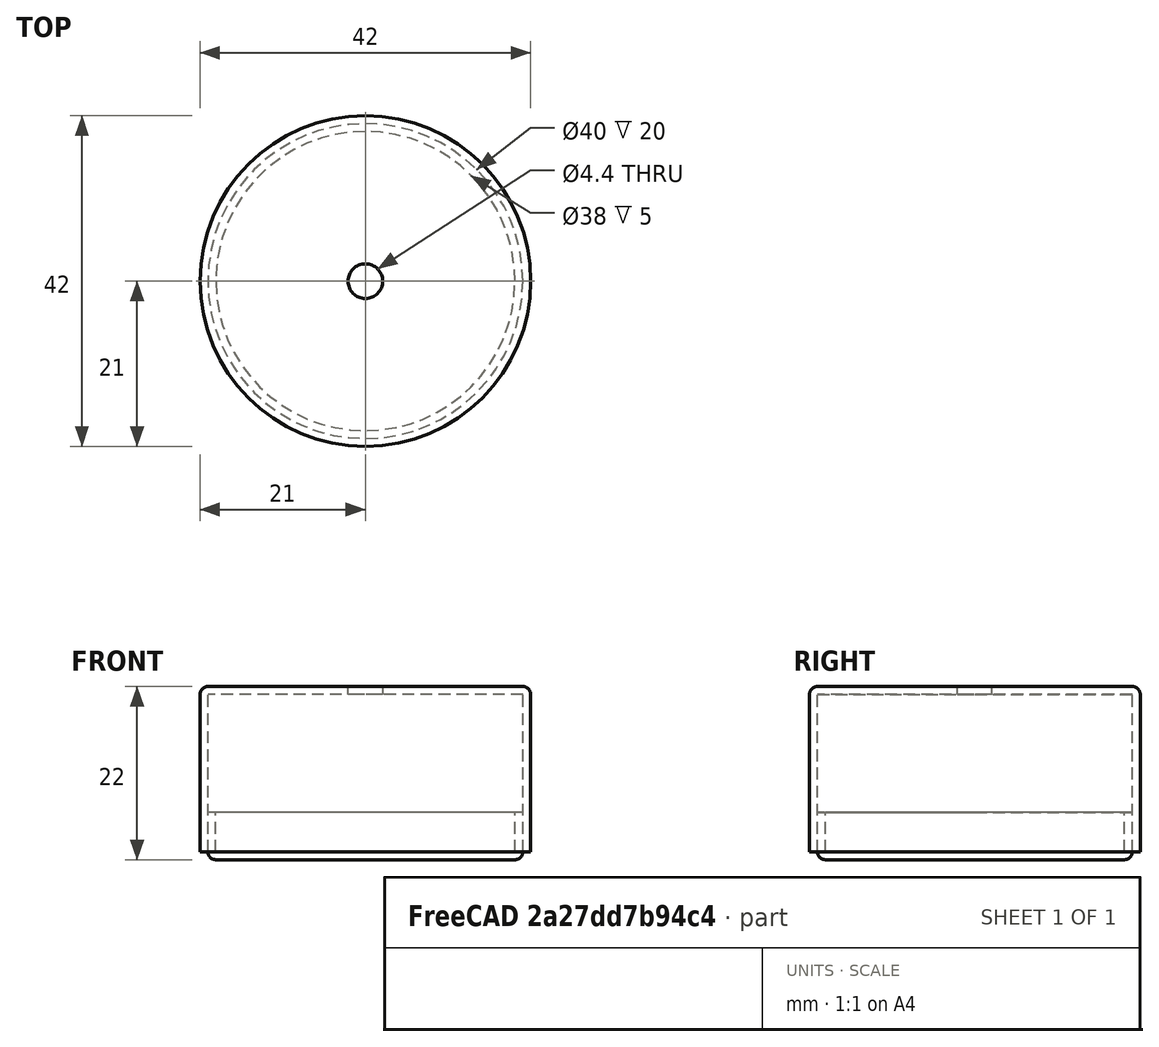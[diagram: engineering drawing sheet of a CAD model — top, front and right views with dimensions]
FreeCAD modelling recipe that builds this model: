
FCSTD DOCUMENT  (FreeCAD 0.19R)
Label: led_kerzenlicht
License: All rights reserved
LicenseURL: http://en.wikipedia.org/wiki/All_rights_reserved
objects: PartDesign::AdditiveCylinder×2, PartDesign::Thickness×2, PartDesign::Body×2, Sketcher::SketchObject×1, PartDesign::Pocket×1
note: 13 computed .brp shape members not serialized (recipe doc carries the construction recipe); baked Part::Feature solids carry a one-line shape summary decoded from their .brp

FEATURE [PartDesign::AdditiveCylinder] Cylinder
  Angle = 360
  AttacherType = Attacher::AttachEngine3D
  Height = 20
  Radius = 20
  Refine = true
FEATURE [PartDesign::Thickness] Thickness
  Base = -> Cylinder [Face3]
  BaseFeature = -> Cylinder
  Intersection = false
  Join = 0
  Mode = 0
  Refine = true
  SupportTransform = false
  Value = 1
FEATURE [Sketcher::SketchObject] Sketch
  FullyConstrained = true
  MapMode = 5
  Placement = pos=(0,0,21) rot=(0,0,1;0rad)
  Support = -> [Thickness]
  sketch-geometry (1):
    g0: Circle CenterX=0 CenterY=0 CenterZ=0 NormalX=0 NormalY=0 NormalZ=1 AngleXU=0 Radius=2.2
  constraints (2):
    c: Radius(g0) = 2.2
    c: Coincident(g0,g-1)
FEATURE [PartDesign::Pocket] Pocket
  BaseFeature = -> Thickness
  Length = 5
  Length2 = 100
  Profile = -> Sketch
  Refine = true
  Type = 1
FEATURE [PartDesign::Body] Body
  Group = -> [Cylinder,Thickness,Sketch,Pocket]
  Origin = -> Origin
  Tip = -> Pocket
FEATURE [PartDesign::AdditiveCylinder] Cylinder001
  Angle = 360
  AttacherType = Attacher::AttachEngine3D
  Height = 5
  Radius = 19
  Refine = true
FEATURE [PartDesign::Thickness] Thickness001
  Base = -> Cylinder001 [Face2]
  BaseFeature = -> Cylinder001
  Intersection = false
  Join = 0
  Mode = 0
  Refine = true
  SupportTransform = false
  Value = 1
FEATURE [PartDesign::Body] Body001
  Group = -> [Cylinder001,Thickness001]
  Origin = -> Origin001
  Tip = -> Thickness001
